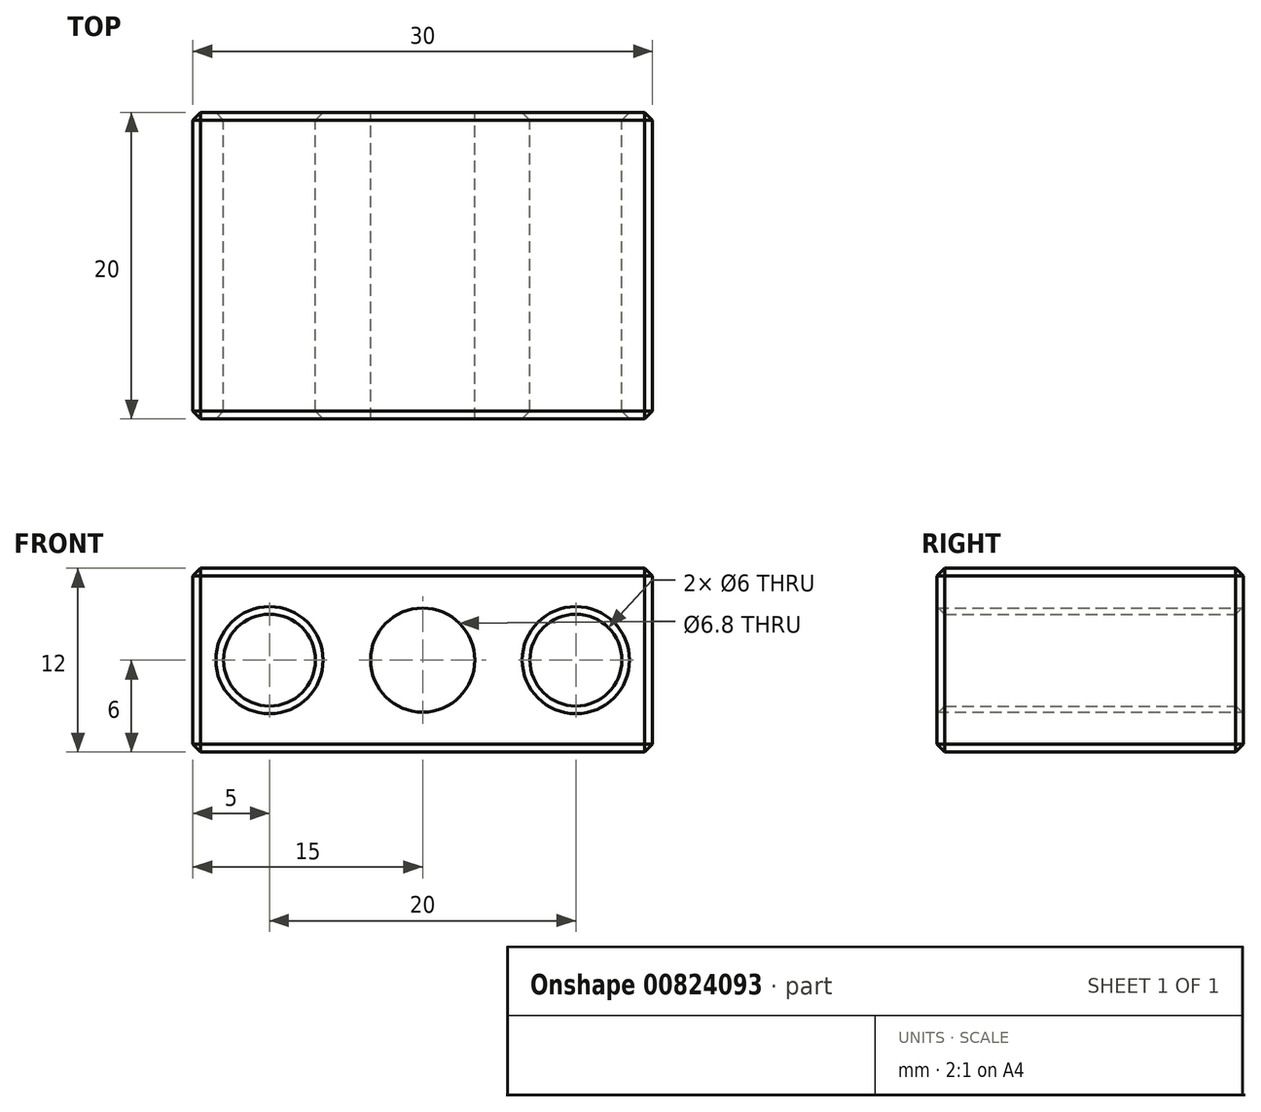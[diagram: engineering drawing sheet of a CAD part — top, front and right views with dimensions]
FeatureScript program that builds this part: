
annotation { "Feature Type Name" : "Feature", "Feature Type Description" : "" }
export const myFeature = defineFeature(function(context is Context, id is Id, definition is map)
    precondition{}
    {
        {
            var Q0;
            Q0=qCreatedBy(makeId("Front.planeOp"),FACE);
            var sketch = newSketch(context, id + "F0", { "sketchPlane" : qUnion([Q0])});
            skLineSegment(sketch, "E0.bottom", {"start": v(15, 6) * mm, "end": v(-15, 6) * mm});
            skLineSegment(sketch, "E0.top", {"start": v(15, -6) * mm, "end": v(-15, -6) * mm});
            skLineSegment(sketch, "E0.left", {"start": v(15, 6) * mm, "end": v(15, -6) * mm});
            skLineSegment(sketch, "E0.right", {"start": v(-15, 6) * mm, "end": v(-15, -6) * mm});
            skPoint(sketch, "E0.middle", {"position": v(0, 0) * mm});
            skLineSegment(sketch, "E1", {"start": v(0, 0) * mm, "end": v(-10, 0) * mm, "construction": true});
            skLineSegment(sketch, "E2", {"start": v(0, 0) * mm, "end": v(10, 0) * mm, "construction": true});
            skCircle(sketch, "E3", {"center": v(0, 0) * mm, "radius": 3.4 * mm});
            skCircle(sketch, "E4", {"center": v(-10, 0) * mm, "radius": 3 * mm});
            skCircle(sketch, "E5", {"center": v(10, 0) * mm, "radius": 3 * mm});
            skCircle(sketch, "E6", {"center": v(0, 0) * mm, "radius": 4 * mm, "construction": true});
            skSolve(sketch);
        }
        {
            var Q0;
            Q0=makeQuery(id+"F0.imprint","IMPRINT",FACE,{"disambiguationData":[TD([[makeQuery(id+"F0.imprint","IMPRINT",EDGE,{"derivedFrom":sQuery(id+"F0.wireOp",EDGE,"E0.bottom")}),1.0]])]});
            var Q1;
            Q1=makeQuery(id+"F0.imprint","IMPRINT",FACE,{"disambiguationData":[TD([[makeQuery(id+"F0.imprint","IMPRINT",EDGE,{"derivedFrom":sQuery(id+"F0.wireOp",EDGE,"E3")}),1.0]])]});
            extrude(context, id + "F1", {"entities" : qUnion([Q0, Q1]), "depth" : 20 * mm, "offsetDistance" : 25 * mm});
        }
        {
            var Q0;
            Q0=sQuery(id+"F0.wireOp",VERTEX,"E0.middle");
            var Q1;
            Q1=makeQuery(id+"F1.opExtrude","SWEPT_BODY",BODY,{"disambiguationData":[OSD([sQuery(id+"F0.wireOp",EDGE,"E0.bottom"),sQuery(id+"F0.wireOp",EDGE,"E0.top"),sQuery(id+"F0.wireOp",EDGE,"E0.left"),sQuery(id+"F0.wireOp",EDGE,"E0.right"),sQuery(id+"F0.wireOp",EDGE,"E4"),sQuery(id+"F0.wireOp",EDGE,"E5")])]});
            hole(context, id + "F2", {"style" : HoleStyle.SIMPLE, "endStyle" : HoleEndStyle.BLIND, "oppositeDirection" : true, "standardTappedOrClearance" : lookupTablePath({ "standard" : "ISO", "engagement" : "75%", "pitch" : "1.25 mm", "size" : "M8", "type" : "Tapped" }), "standardBlindInLast" : lookupTablePath({ "standard" : "ISO", "engagement" : "75%", "pitch" : "1.25 mm", "size" : "M8", "type" : "Tapped" }), "holeDiameter" : 6.8 * mm, "majorDiameter" : 8 * mm, "showTappedDepth" : true, "holeDepth" : 23.75 * mm, "isTappedThrough" : true, "tappedDepth" : 20 * mm, "tapClearance" : 3, "startFromSketch" : true, "locations" : qUnion([Q0]), "scope" : qUnion([Q1])});
        }
        {
            var Q0;
            Q0=makeQuery(id+"F1.opExtrude","SWEPT_FACE",FACE,{"disambiguationData":[OSD([sQuery(id+"F0.wireOp",EDGE,"E0.bottom")])]});
            var Q1;
            Q1=makeQuery(id+"F1.opExtrude","SWEPT_FACE",FACE,{"disambiguationData":[OSD([sQuery(id+"F0.wireOp",EDGE,"E0.top")])]});
            var Q2;
            Q2=makeQuery(id+"F1.opExtrude","SWEPT_FACE",FACE,{"disambiguationData":[OSD([sQuery(id+"F0.wireOp",EDGE,"E0.right")])]});
            var Q3;
            Q3=makeQuery(id+"F1.opExtrude","SWEPT_FACE",FACE,{"disambiguationData":[OSD([sQuery(id+"F0.wireOp",EDGE,"E0.left")])]});
            var Q4;
            Q4=makeQuery(id+"F1.opExtrude","SWEPT_FACE",FACE,{"disambiguationData":[OSD([sQuery(id+"F0.wireOp",EDGE,"E4")])]});
            var Q5;
            Q5=makeQuery(id+"F1.opExtrude","SWEPT_FACE",FACE,{"disambiguationData":[OSD([sQuery(id+"F0.wireOp",EDGE,"E3")])]});
            var Q6;
            Q6=makeQuery(id+"F1.opExtrude","SWEPT_FACE",FACE,{"disambiguationData":[OSD([sQuery(id+"F0.wireOp",EDGE,"E5")])]});
            var Q7;
            Q7=makeQuery(id+"F2.hole-0.boolean.opBoolean","COPY",FACE,{"derivedFrom":makeQuery(id+"F2.hole-0.opRevolve","SWEPT_FACE",FACE,{"disambiguationData":[OSD([sQuery(id+"F2.hole-0.sketch.wireOp",EDGE,"core_line_2")])]})});
            chamfer(context, id + "F3", {"entities" : qUnion([Q0, Q1, Q2, Q3, Q4, Q5, Q6, Q7]), "width" : 0.5 * mm, "tangentPropagation" : true});
        }
    });
